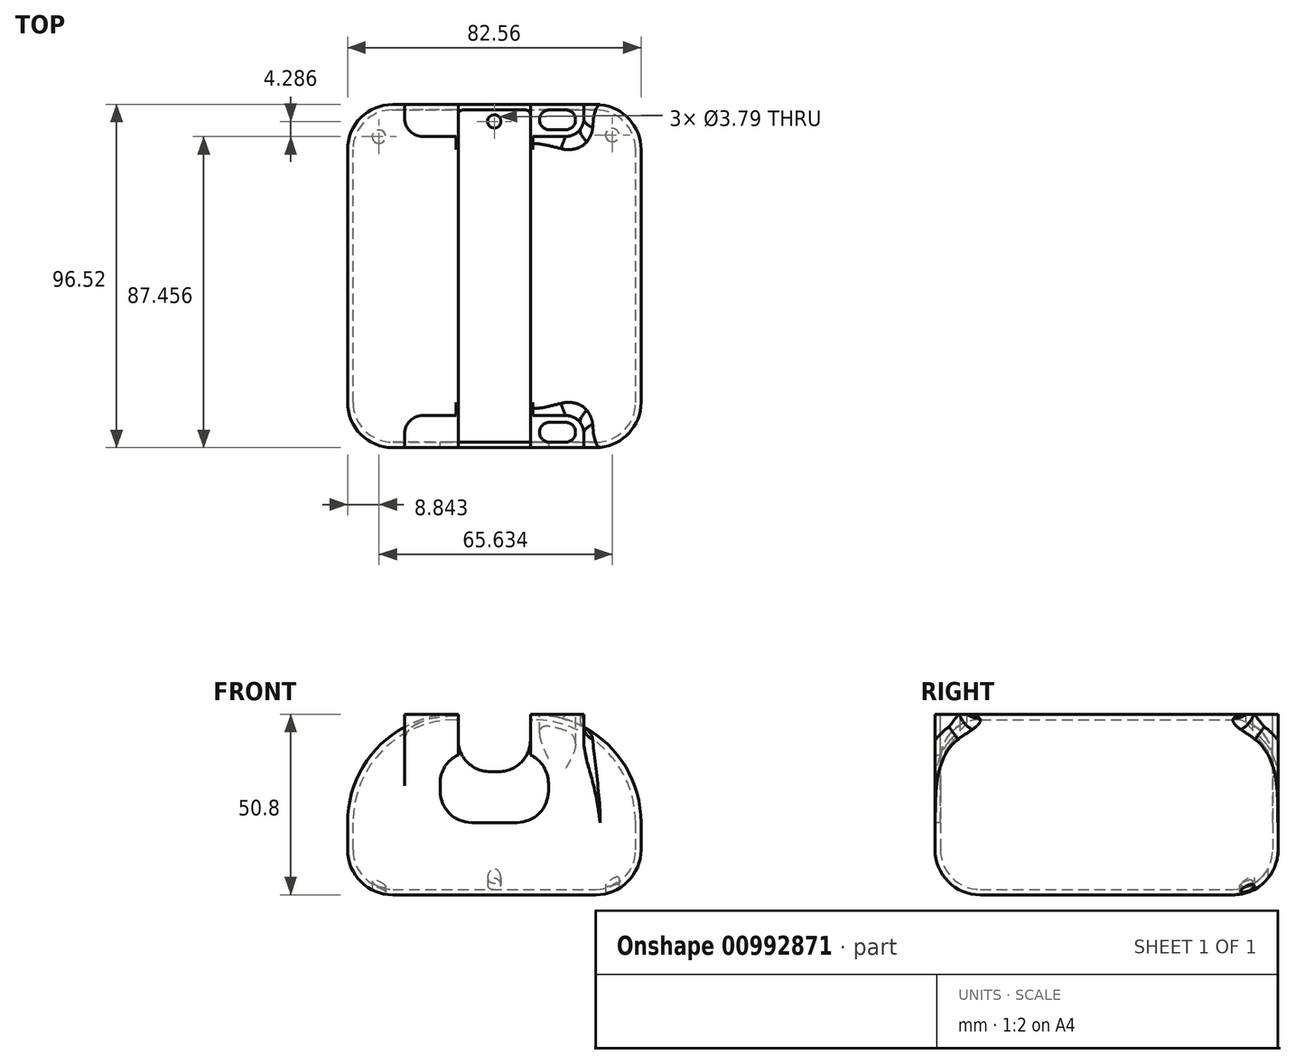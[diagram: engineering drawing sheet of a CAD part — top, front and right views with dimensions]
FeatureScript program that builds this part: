
annotation { "Feature Type Name" : "Feature", "Feature Type Description" : "" }
export const myFeature = defineFeature(function(context is Context, id is Id, definition is map)
    precondition{}
    {
        {
            var Q0;
            Q0=qCreatedBy(makeId("Top.planeOp"),FACE);
            var sketch = newSketch(context, id + "F0", { "sketchPlane" : qUnion([Q0])});
            skLineSegment(sketch, "E0.bottom", {"start": v(41.28, 0) * mm, "end": v(-41.28, 0) * mm});
            skLineSegment(sketch, "E0.top", {"start": v(41.28, 114.3) * mm, "end": v(-41.28, 114.3) * mm});
            skLineSegment(sketch, "E0.left", {"start": v(41.28, 0) * mm, "end": v(41.28, 114.3) * mm});
            skLineSegment(sketch, "E0.right", {"start": v(-41.28, 0) * mm, "end": v(-41.28, 114.3) * mm});
            skPoint(sketch, "E0.middle", {"position": v(0, 57.15) * mm});
            skSolve(sketch);
        }
        {
            var Q0;
            Q0=makeQuery(id+"F0.imprint","IMPRINT",FACE,{"disambiguationData":[TD([[makeQuery(id+"F0.imprint","IMPRINT",EDGE,{"derivedFrom":sQuery(id+"F0.wireOp",EDGE,"E0.bottom")}),-1.0]])]});
            extrude(context, id + "F1", {"entities" : qUnion([Q0]), "depth" : 50.8 * mm, "offsetDistance" : 25.4 * mm});
        }
        {
            var Q0;
            Q0=makeQuery(id+"F1.opExtrude","CAP_EDGE",EDGE,{"disambiguationData":[OSD([sQuery(id+"F0.wireOp",EDGE,"E0.left")])],"isStart":false});
            var Q1;
            Q1=makeQuery(id+"F1.opExtrude","CAP_EDGE",EDGE,{"disambiguationData":[OSD([sQuery(id+"F0.wireOp",EDGE,"E0.right")])],"isStart":false});
            fillet(context, id + "F2", {"entities" : qUnion([Q0, Q1]), "radius" : 30.48 * mm, "tangentPropagation" : true, "allowEdgeOverflow" : false});
        }
        {
            var Q0;
            Q0=makeQuery(id+"F1.opExtrude","SWEPT_FACE",FACE,{"disambiguationData":[OSD([sQuery(id+"F0.wireOp",EDGE,"E0.left")])]});
            var Q1;
            Q1=makeQuery(id+"F1.opExtrude","SWEPT_FACE",FACE,{"disambiguationData":[OSD([sQuery(id+"F0.wireOp",EDGE,"E0.right")])]});
            var Q2;
            Q2=makeQuery(id+"F1.opExtrude","CAP_EDGE",EDGE,{"disambiguationData":[OSD([sQuery(id+"F0.wireOp",EDGE,"E0.top")])],"isStart":true});
            var Q3;
            Q3=makeQuery(id+"F1.opExtrude","CAP_EDGE",EDGE,{"disambiguationData":[OSD([sQuery(id+"F0.wireOp",EDGE,"E0.bottom")])],"isStart":true});
            var Q4;
            Q4=makeQuery(id+"F1.opExtrude","CAP_EDGE",EDGE,{"disambiguationData":[OSD([sQuery(id+"F0.wireOp",EDGE,"E0.top")])],"isStart":false});
            fillet(context, id + "F3", {"entities" : qUnion([Q0, Q1, Q2, Q3, Q4]), "radius" : 12.7 * mm, "tangentPropagation" : true, "allowEdgeOverflow" : false});
        }
        {
            var Q0;
            {var subQ0=sQuery(id+"F0.wireOp",EDGE,"E0.right");var subQ1=sQuery(id+"F0.wireOp",EDGE,"E0.left");var subQ2=sQuery(id+"F0.wireOp",EDGE,"E0.top");var subQ3=sQuery(id+"F0.wireOp",EDGE,"E0.bottom");Q0=makeQuery(id+"F4FyCP3RIGp18HZ_1.splitOp","SPLIT_SURFACE_INTERSECT",FACE,{"derivedFrom":[makeQuery(id+"F3.opFillet","BLEND_FACE",FACE,{"disambiguationData":[OSD([subQ1]),TDD([makeQuery(id+"F1.opExtrude","CAP_EDGE",EDGE,{"disambiguationData":[OSD([subQ1])],"isStart":true})])]}),makeQuery(id+"F3.opFillet","BLEND_FACE",FACE,{"disambiguationData":[OSD([subQ1]),TDD([makeQuery(id+"F1.opExtrude","CAP_EDGE",EDGE,{"disambiguationData":[OSD([subQ1])],"isStart":false})])]}),makeQuery(id+"F3.opFillet","BLEND_FACE",FACE,{"disambiguationData":[OSD([subQ0]),TDD([makeQuery(id+"F1.opExtrude","CAP_EDGE",EDGE,{"disambiguationData":[OSD([subQ0])],"isStart":true})])]}),makeQuery(id+"F3.opFillet","BLEND_FACE",FACE,{"disambiguationData":[OSD([subQ0]),TDD([makeQuery(id+"F1.opExtrude","CAP_EDGE",EDGE,{"disambiguationData":[OSD([subQ0])],"isStart":false})])]}),makeQuery(id+"F1.opExtrude","CAP_FACE",FACE,{"disambiguationData":[OSD([subQ3,subQ2,subQ1,subQ0])],"isStart":true}),makeQuery(id+"F1.opExtrude","CAP_FACE",FACE,{"disambiguationData":[OSD([subQ3,subQ2,subQ1,subQ0])],"isStart":false}),makeQuery(id+"F1.opExtrude","SWEPT_FACE",FACE,{"disambiguationData":[OSD([subQ1])]}),makeQuery(id+"F1.opExtrude","SWEPT_FACE",FACE,{"disambiguationData":[OSD([subQ0])]})],"isFromBackBody":true});}
            var Q1;
            Q1=makeQuery(id+"F1.opExtrude","SWEPT_BODY",BODY,{"disambiguationData":[OSD([sQuery(id+"F0.wireOp",EDGE,"E0.bottom"),sQuery(id+"F0.wireOp",EDGE,"E0.top"),sQuery(id+"F0.wireOp",EDGE,"E0.left"),sQuery(id+"F0.wireOp",EDGE,"E0.right")])]});
            shell(context, id + "F4", {"isHollow" : true, "entities" : qUnion([Q0]), "parts" : qUnion([Q1]), "thickness" : 1.52 * mm});
        }
        {
            var Q0;
            Q0=makeQuery(id+"F4FyCP3RIGp18HZ_1.splitOp","SPLIT",FACE,{"derivedFrom":makeQuery(id+"F1.opExtrude","CAP_FACE",FACE,{"disambiguationData":[OSD([sQuery(id+"F0.wireOp",EDGE,"E0.bottom"),sQuery(id+"F0.wireOp",EDGE,"E0.top"),sQuery(id+"F0.wireOp",EDGE,"E0.left"),sQuery(id+"F0.wireOp",EDGE,"E0.right")])],"isStart":false}),"isFromBackBody":true});
            var sketch = newSketch(context, id + "F5", { "sketchPlane" : qUnion([Q0])});
            skLineSegment(sketch, "E1.bottom", {"start": v(12.7, 7.11) * mm, "end": v(22.86, 7.11) * mm});
            skLineSegment(sketch, "E1.top", {"start": v(12.7, 1.52) * mm, "end": v(22.86, 1.52) * mm});
            skLineSegment(sketch, "E1.left", {"start": v(12.7, 7.11) * mm, "end": v(12.7, 1.52) * mm});
            skLineSegment(sketch, "E1.right", {"start": v(22.86, 7.11) * mm, "end": v(22.86, 1.52) * mm});
            skSolve(sketch);
        }
        {
            var Q0;
            {var subQ0=sQuery(id+"F0.wireOp",EDGE,"E0.right");var subQ1=sQuery(id+"F0.wireOp",EDGE,"E0.left");var subQ2=sQuery(id+"F0.wireOp",EDGE,"E0.top");var subQ3=sQuery(id+"F0.wireOp",EDGE,"E0.bottom");var subQ4=makeQuery(id+"F1.opExtrude","CAP_FACE",FACE,{"disambiguationData":[OSD([subQ3,subQ2,subQ1,subQ0])],"isStart":false});var subQ5=subQ4;Q0=makeQuery(id+"F5.imprint","IMPRINT",FACE,{"disambiguationData":[TD([[makeQuery(id+"F5.imprint","IMPRINT",EDGE,{"derivedFrom":makeQuery(id+"F3.opFillet","BLEND_EDGE",EDGE,{"blendedFrom":[makeQuery(id+"F1.opExtrude","CAP_EDGE",EDGE,{"disambiguationData":[OSD([subQ3])],"isStart":false}),subQ5],"blendedInto":[subQ5]})}),1.0]])]});}
            var sketch = newSketch(context, id + "F6", { "sketchPlane" : qUnion([Q0])});
            skLineSegment(sketch, "E2.bottom", {"start": v(25.2, 0) * mm, "end": v(-25.2, 0) * mm});
            skLineSegment(sketch, "E2.top", {"start": v(25.2, 9.01) * mm, "end": v(10.8, 9.01) * mm});
            skLineSegment(sketch, "E2.left", {"start": v(25.2, 0) * mm, "end": v(25.2, 9.01) * mm});
            skLineSegment(sketch, "E2.right", {"start": v(-25.2, 0) * mm, "end": v(-25.2, 9.01) * mm});
            skPoint(sketch, "E2.middle", {"position": v(0, 4.5) * mm});
            skLineSegment(sketch, "E3.bottom", {"start": v(-10.8, 20.98) * mm, "end": v(10.8, 20.98) * mm});
            skLineSegment(sketch, "E3.left", {"start": v(-10.8, 20.98) * mm, "end": v(-10.8, 9.01) * mm});
            skLineSegment(sketch, "E3.right", {"start": v(10.8, 20.98) * mm, "end": v(10.8, 9.01) * mm});
            skLineSegment(sketch, "E4.trimOffspring", {"start": v(-10.8, 9.01) * mm, "end": v(-25.2, 9.01) * mm});
            skSolve(sketch);
        }
        {
            var Q0;
            Q0=makeQuery(id+"F6.imprint","IMPRINT",FACE,{"disambiguationData":[TD([[makeQuery(id+"F6.imprint","IMPRINT",EDGE,{"derivedFrom":sQuery(id+"F6.wireOp",EDGE,"E2.bottom")}),-1.0]])]});
            extrude(context, id + "F7", {"entities" : qUnion([Q0]), "operationType" : NewBodyOperationType.ADD, "endBound" : BoundingType.UP_TO_NEXT, "oppositeDirection" : true, "depth" : 25.4 * mm, "offsetDistance" : 25.4 * mm});
        }
        {
            var Q0;
            Q0=qSketchRegion(id+"F5",true);
            extrude(context, id + "F8", {"entities" : qUnion([Q0]), "operationType" : NewBodyOperationType.REMOVE, "oppositeDirection" : true, "depth" : 25.4 * mm, "offsetDistance" : 25.4 * mm});
        }
        {
            var Q0;
            Q0=makeQuery(id+"F8.boolean.opBoolean","COPY",EDGE,{"derivedFrom":makeQuery(id+"F8.opExtrude","SWEPT_EDGE",EDGE,{"disambiguationData":[OSD([sQuery(id+"F5.wireOp",EDGE,"E1.bottom"),sQuery(id+"F5.wireOp",EDGE,"E1.left")])]})});
            var Q1;
            Q1=makeQuery(id+"FyfUCAUJJe16imM_1.1.F8.boolean.opBoolean","COPY",EDGE,{"derivedFrom":makeQuery(id+"FyfUCAUJJe16imM_1.1.F8.opExtrude","SWEPT_EDGE",EDGE,{"disambiguationData":[OSD([sQuery(id+"F5.wireOp",EDGE,"E1.bottom"),sQuery(id+"F5.wireOp",EDGE,"E1.right")])]})});
            var Q2;
            Q2=makeQuery(id+"FyfUCAUJJe16imM_1.1.F8.boolean.opBoolean","COPY",EDGE,{"derivedFrom":makeQuery(id+"FyfUCAUJJe16imM_1.1.F8.opExtrude","SWEPT_EDGE",EDGE,{"disambiguationData":[OSD([sQuery(id+"F5.wireOp",EDGE,"E1.top"),sQuery(id+"F5.wireOp",EDGE,"E1.right")])]})});
            var Q3;
            Q3=makeQuery(id+"F8.boolean.opBoolean","COPY",EDGE,{"derivedFrom":makeQuery(id+"F8.opExtrude","SWEPT_EDGE",EDGE,{"disambiguationData":[OSD([sQuery(id+"F5.wireOp",EDGE,"E1.top"),sQuery(id+"F5.wireOp",EDGE,"E1.left")])]})});
            var Q4;
            Q4=makeQuery(id+"F8.boolean.opBoolean","COPY",EDGE,{"derivedFrom":makeQuery(id+"F8.opExtrude","SWEPT_EDGE",EDGE,{"disambiguationData":[OSD([sQuery(id+"F5.wireOp",EDGE,"E1.top"),sQuery(id+"F5.wireOp",EDGE,"E1.right")])]})});
            var Q5;
            Q5=makeQuery(id+"FyfUCAUJJe16imM_1.1.F8.boolean.opBoolean","COPY",EDGE,{"derivedFrom":makeQuery(id+"FyfUCAUJJe16imM_1.1.F8.opExtrude","SWEPT_EDGE",EDGE,{"disambiguationData":[OSD([sQuery(id+"F5.wireOp",EDGE,"E1.top"),sQuery(id+"F5.wireOp",EDGE,"E1.left")])]})});
            var Q6;
            Q6=makeQuery(id+"FyfUCAUJJe16imM_1.1.F8.boolean.opBoolean","COPY",EDGE,{"derivedFrom":makeQuery(id+"FyfUCAUJJe16imM_1.1.F8.opExtrude","SWEPT_EDGE",EDGE,{"disambiguationData":[OSD([sQuery(id+"F5.wireOp",EDGE,"E1.bottom"),sQuery(id+"F5.wireOp",EDGE,"E1.left")])]})});
            var Q7;
            Q7=makeQuery(id+"F8.boolean.opBoolean","COPY",EDGE,{"derivedFrom":makeQuery(id+"F8.opExtrude","SWEPT_EDGE",EDGE,{"disambiguationData":[OSD([sQuery(id+"F5.wireOp",EDGE,"E1.bottom"),sQuery(id+"F5.wireOp",EDGE,"E1.right")])]})});
            fillet(context, id + "F9", {"entities" : qUnion([Q0, Q1, Q2, Q3, Q4, Q5, Q6, Q7]), "radius" : 2.8 * mm, "tangentPropagation" : true, "allowEdgeOverflow" : false});
        }
        {
            var Q0;
            Q0=qCreatedBy(makeId("Right.planeOp"),FACE);
            var sketch = newSketch(context, id + "F10", { "sketchPlane" : qUnion([Q0])});
            skLineSegment(sketch, "E5.bottom", {"start": v(48.26, 57.67) * mm, "end": v(127.56, 57.67) * mm});
            skLineSegment(sketch, "E5.top", {"start": v(48.26, -8) * mm, "end": v(127.56, -8) * mm});
            skLineSegment(sketch, "E5.left", {"start": v(48.26, 57.67) * mm, "end": v(48.26, -8) * mm});
            skLineSegment(sketch, "E5.right", {"start": v(127.56, 57.67) * mm, "end": v(127.56, -8) * mm});
            skSolve(sketch);
        }
        {
            var Q0;
            Q0=qSketchRegion(id+"F10",true);
            extrude(context, id + "F11", {"entities" : qUnion([Q0]), "operationType" : NewBodyOperationType.REMOVE, "endBound" : BoundingType.SYMMETRIC, "oppositeDirection" : true, "depth" : 127 * mm, "offsetDistance" : 25.4 * mm});
        }
        {
            var Q0;
            Q0=makeQuery(id+"F1.opExtrude","SWEPT_BODY",BODY,{"disambiguationData":[OSD([sQuery(id+"F0.wireOp",EDGE,"E0.bottom"),sQuery(id+"F0.wireOp",EDGE,"E0.top"),sQuery(id+"F0.wireOp",EDGE,"E0.left"),sQuery(id+"F0.wireOp",EDGE,"E0.right")])]});
            var Q1;
            Q1=makeQuery(id+"F11.boolean.opBoolean","COPY",FACE,{"derivedFrom":makeQuery(id+"F11.opExtrude","SWEPT_FACE",FACE,{"disambiguationData":[OSD([sQuery(id+"F10.wireOp",EDGE,"E5.left")])]})});
            mirror(context, id + "F12", {"operationType" : NewBodyOperationType.ADD, "entities" : qUnion([Q0]), "mirrorPlane" : qUnion([Q1])});
        }
        {
            var Q0;
            Q0=qCreatedBy(makeId("Front.planeOp"),FACE);
            var sketch = newSketch(context, id + "F13", { "sketchPlane" : qUnion([Q0])});
            skLineSegment(sketch, "E6.bottom", {"start": v(15.24, 39.37) * mm, "end": v(-15.24, 39.37) * mm});
            skLineSegment(sketch, "E6.top", {"start": v(15.24, 20.32) * mm, "end": v(-15.24, 20.32) * mm});
            skLineSegment(sketch, "E6.left", {"start": v(15.24, 39.37) * mm, "end": v(15.24, 20.32) * mm});
            skLineSegment(sketch, "E6.right", {"start": v(-15.24, 39.37) * mm, "end": v(-15.24, 20.32) * mm});
            skPoint(sketch, "E6.middle", {"position": v(0, 29.85) * mm});
            skSolve(sketch);
        }
        {
            var Q0;
            Q0=qSketchRegion(id+"F13",true);
            extrude(context, id + "F14", {"entities" : qUnion([Q0]), "operationType" : NewBodyOperationType.REMOVE, "oppositeDirection" : true, "depth" : 25.4 * mm, "offsetDistance" : 25.4 * mm});
        }
        {
            var Q0;
            Q0=qCreatedBy(makeId("Top.planeOp"),FACE);
            var sketch = newSketch(context, id + "F15", { "sketchPlane" : qUnion([Q0])});
            skCircle(sketch, "E7", {"center": v(33.2, 87.95) * mm, "radius": 1.9 * mm});
            skCircle(sketch, "E8", {"center": v(-32.44, 87.46) * mm, "radius": 1.9 * mm});
            skCircle(sketch, "E9", {"center": v(0, 91.74) * mm, "radius": 1.9 * mm});
            skSolve(sketch);
        }
        {
            var Q0;
            Q0=qSketchRegion(id+"F15",true);
            extrude(context, id + "F16", {"entities" : qUnion([Q0]), "operationType" : NewBodyOperationType.REMOVE, "depth" : 25.4 * mm, "offsetDistance" : 25.4 * mm});
        }
        {
            var Q0;
            Q0=qCreatedBy(makeId("Front.planeOp"),FACE);
            var sketch = newSketch(context, id + "F17", { "sketchPlane" : qUnion([Q0])});
            skLineSegment(sketch, "E10.bottom", {"start": v(10.16, 34.66) * mm, "end": v(-10.16, 34.66) * mm});
            skLineSegment(sketch, "E10.top", {"start": v(10.16, 131.65) * mm, "end": v(-10.16, 131.65) * mm});
            skLineSegment(sketch, "E10.left", {"start": v(10.16, 34.66) * mm, "end": v(10.16, 131.65) * mm});
            skLineSegment(sketch, "E10.right", {"start": v(-10.16, 34.66) * mm, "end": v(-10.16, 131.65) * mm});
            skPoint(sketch, "E10.middle", {"position": v(0, 83.15) * mm});
            skSolve(sketch);
        }
        {
            var Q0;
            Q0=qSketchRegion(id+"F17",true);
            extrude(context, id + "F18", {"entities" : qUnion([Q0]), "operationType" : NewBodyOperationType.REMOVE, "endBound" : BoundingType.THROUGH_ALL, "oppositeDirection" : true, "depth" : 25.4 * mm, "offsetDistance" : 25.4 * mm});
        }
        {
            var Q0;
            Q0=makeQuery(id+"F14.boolean.opBoolean","COPY",EDGE,{"derivedFrom":makeQuery(id+"F14.opExtrude","SWEPT_EDGE",EDGE,{"disambiguationData":[OSD([sQuery(id+"F13.wireOp",EDGE,"E6.top"),sQuery(id+"F13.wireOp",EDGE,"E6.right")])]})});
            var Q1;
            Q1=makeQuery(id+"F14.boolean.opBoolean","COPY",EDGE,{"derivedFrom":makeQuery(id+"F14.opExtrude","SWEPT_EDGE",EDGE,{"disambiguationData":[OSD([sQuery(id+"F13.wireOp",EDGE,"E6.top"),sQuery(id+"F13.wireOp",EDGE,"E6.left")])]})});
            var Q2;
            Q2=makeQuery(id+"F14.boolean.opBoolean","COPY",EDGE,{"derivedFrom":makeQuery(id+"F14.opExtrude","SWEPT_EDGE",EDGE,{"disambiguationData":[OSD([sQuery(id+"F13.wireOp",EDGE,"E6.bottom"),sQuery(id+"F13.wireOp",EDGE,"E6.right")])]})});
            var Q3;
            Q3=makeQuery(id+"F14.boolean.opBoolean","COPY",EDGE,{"derivedFrom":makeQuery(id+"F14.opExtrude","SWEPT_EDGE",EDGE,{"disambiguationData":[OSD([sQuery(id+"F13.wireOp",EDGE,"E6.bottom"),sQuery(id+"F13.wireOp",EDGE,"E6.left")])]})});
            var Q4;
            Q4=makeQuery(id+"F18.boolean.opBoolean","COPY",EDGE,{"derivedFrom":makeQuery(id+"F18.opExtrude","SWEPT_EDGE",EDGE,{"disambiguationData":[OSD([sQuery(id+"F17.wireOp",EDGE,"E10.bottom"),sQuery(id+"F17.wireOp",EDGE,"E10.right")])]})});
            var Q5;
            Q5=makeQuery(id+"F18.boolean.opBoolean","COPY",EDGE,{"derivedFrom":makeQuery(id+"F18.opExtrude","SWEPT_EDGE",EDGE,{"disambiguationData":[OSD([sQuery(id+"F17.wireOp",EDGE,"E10.bottom"),sQuery(id+"F17.wireOp",EDGE,"E10.left")])]})});
            fillet(context, id + "F19", {"entities" : qUnion([Q0, Q1, Q2, Q3, Q4, Q5]), "radius" : 8.9 * mm, "tangentPropagation" : true, "allowEdgeOverflow" : false});
        }
        {
            var Q0;
            Q0=makeQuery(id+"F7.opExtrude","SWEPT_EDGE",EDGE,{"disambiguationData":[OSD([sQuery(id+"F6.wireOp",EDGE,"E2.top"),sQuery(id+"F6.wireOp",EDGE,"E2.left")])]});
            var Q1;
            Q1=makeQuery(id+"F7.opExtrude","SWEPT_EDGE",EDGE,{"disambiguationData":[OSD([sQuery(id+"F6.wireOp",EDGE,"E2.right"),sQuery(id+"F6.wireOp",EDGE,"E4.trimOffspring")])]});
            var Q2;
            Q2=makeQuery(id+"F12.opPattern","COPY",EDGE,{"derivedFrom":makeQuery(id+"F7.opExtrude","SWEPT_EDGE",EDGE,{"disambiguationData":[OSD([sQuery(id+"F6.wireOp",EDGE,"E2.right"),sQuery(id+"F6.wireOp",EDGE,"E4.trimOffspring")])]}),"instanceName":"1"});
            var Q3;
            Q3=makeQuery(id+"F12.opPattern","COPY",EDGE,{"derivedFrom":makeQuery(id+"F7.opExtrude","SWEPT_EDGE",EDGE,{"disambiguationData":[OSD([sQuery(id+"F6.wireOp",EDGE,"E2.top"),sQuery(id+"F6.wireOp",EDGE,"E2.left")])]}),"instanceName":"1"});
            fillet(context, id + "F20", {"entities" : qUnion([Q0, Q1, Q2, Q3]), "radius" : 5.08 * mm, "tangentPropagation" : true, "allowEdgeOverflow" : false});
        }
        {
            var Q0;
            {var subQ0=sQuery(id+"F0.wireOp",EDGE,"E0.bottom");var subQ1=sQuery(id+"F0.wireOp",EDGE,"E0.left");Q0=makeQuery(id+"F20.opFillet","BLEND_EDGE",EDGE,{"blendedFrom":[makeQuery(id+"F7.opExtrude","SWEPT_EDGE",EDGE,{"disambiguationData":[OSD([sQuery(id+"F6.wireOp",EDGE,"E2.top"),sQuery(id+"F6.wireOp",EDGE,"E2.left")])]}),makeQuery(id+"F3.opFillet","BLEND_FACE",FACE,{"disambiguationData":[OSD([subQ0,subQ1]),TDD([makeQuery(id+"F2.opFillet","BLEND_EDGE",EDGE,{"blendedFrom":[makeQuery(id+"F1.opExtrude","CAP_EDGE",EDGE,{"disambiguationData":[OSD([subQ1])],"isStart":false}),makeQuery(id+"F1.opExtrude","SWEPT_FACE",FACE,{"disambiguationData":[OSD([subQ0])]})],"blendedInto":[makeQuery(id+"F1.opExtrude","SWEPT_FACE",FACE,{"disambiguationData":[OSD([subQ0])]})]})])]})],"blendedInto":[makeQuery(id+"F3.opFillet","BLEND_FACE",FACE,{"disambiguationData":[OSD([subQ0,subQ1]),TDD([makeQuery(id+"F2.opFillet","BLEND_EDGE",EDGE,{"blendedFrom":[makeQuery(id+"F1.opExtrude","CAP_EDGE",EDGE,{"disambiguationData":[OSD([subQ1])],"isStart":false}),makeQuery(id+"F1.opExtrude","SWEPT_FACE",FACE,{"disambiguationData":[OSD([subQ0])]})],"blendedInto":[makeQuery(id+"F1.opExtrude","SWEPT_FACE",FACE,{"disambiguationData":[OSD([subQ0])]})]})])]})]});}
            var Q1;
            Q1=makeQuery(id+"F7.opExtrude","CAP_EDGE",EDGE,{"disambiguationData":[OSD([sQuery(id+"F6.wireOp",EDGE,"E4.trimOffspring")])],"isStart":false});
            var Q2;
            {var subQ0=sQuery(id+"F0.wireOp",EDGE,"E0.bottom");var subQ1=sQuery(id+"F0.wireOp",EDGE,"E0.left");Q2=makeQuery(id+"F20.opFillet","BLEND_EDGE",EDGE,{"blendedFrom":[makeQuery(id+"F12.opPattern","COPY",EDGE,{"derivedFrom":makeQuery(id+"F7.opExtrude","SWEPT_EDGE",EDGE,{"disambiguationData":[OSD([sQuery(id+"F6.wireOp",EDGE,"E2.top"),sQuery(id+"F6.wireOp",EDGE,"E2.left")])]}),"instanceName":"1"}),makeQuery(id+"F12.opPattern","COPY",FACE,{"derivedFrom":makeQuery(id+"F3.opFillet","BLEND_FACE",FACE,{"disambiguationData":[OSD([subQ0,subQ1]),TDD([makeQuery(id+"F2.opFillet","BLEND_EDGE",EDGE,{"blendedFrom":[makeQuery(id+"F1.opExtrude","CAP_EDGE",EDGE,{"disambiguationData":[OSD([subQ1])],"isStart":false}),makeQuery(id+"F1.opExtrude","SWEPT_FACE",FACE,{"disambiguationData":[OSD([subQ0])]})],"blendedInto":[makeQuery(id+"F1.opExtrude","SWEPT_FACE",FACE,{"disambiguationData":[OSD([subQ0])]})]})])]}),"instanceName":"1"})],"blendedInto":[makeQuery(id+"F12.opPattern","COPY",FACE,{"derivedFrom":makeQuery(id+"F3.opFillet","BLEND_FACE",FACE,{"disambiguationData":[OSD([subQ0,subQ1]),TDD([makeQuery(id+"F2.opFillet","BLEND_EDGE",EDGE,{"blendedFrom":[makeQuery(id+"F1.opExtrude","CAP_EDGE",EDGE,{"disambiguationData":[OSD([subQ1])],"isStart":false}),makeQuery(id+"F1.opExtrude","SWEPT_FACE",FACE,{"disambiguationData":[OSD([subQ0])]})],"blendedInto":[makeQuery(id+"F1.opExtrude","SWEPT_FACE",FACE,{"disambiguationData":[OSD([subQ0])]})]})])]}),"instanceName":"1"})]});}
            var Q3;
            Q3=makeQuery(id+"F12.opPattern","COPY",EDGE,{"derivedFrom":makeQuery(id+"F7.opExtrude","CAP_EDGE",EDGE,{"disambiguationData":[OSD([sQuery(id+"F6.wireOp",EDGE,"E4.trimOffspring")])],"isStart":false}),"instanceName":"1"});
            fillet(context, id + "F21", {"entities" : qUnion([Q0, Q1, Q2, Q3]), "radius" : 5.08 * mm, "tangentPropagation" : true, "allowEdgeOverflow" : false});
        }
    });
